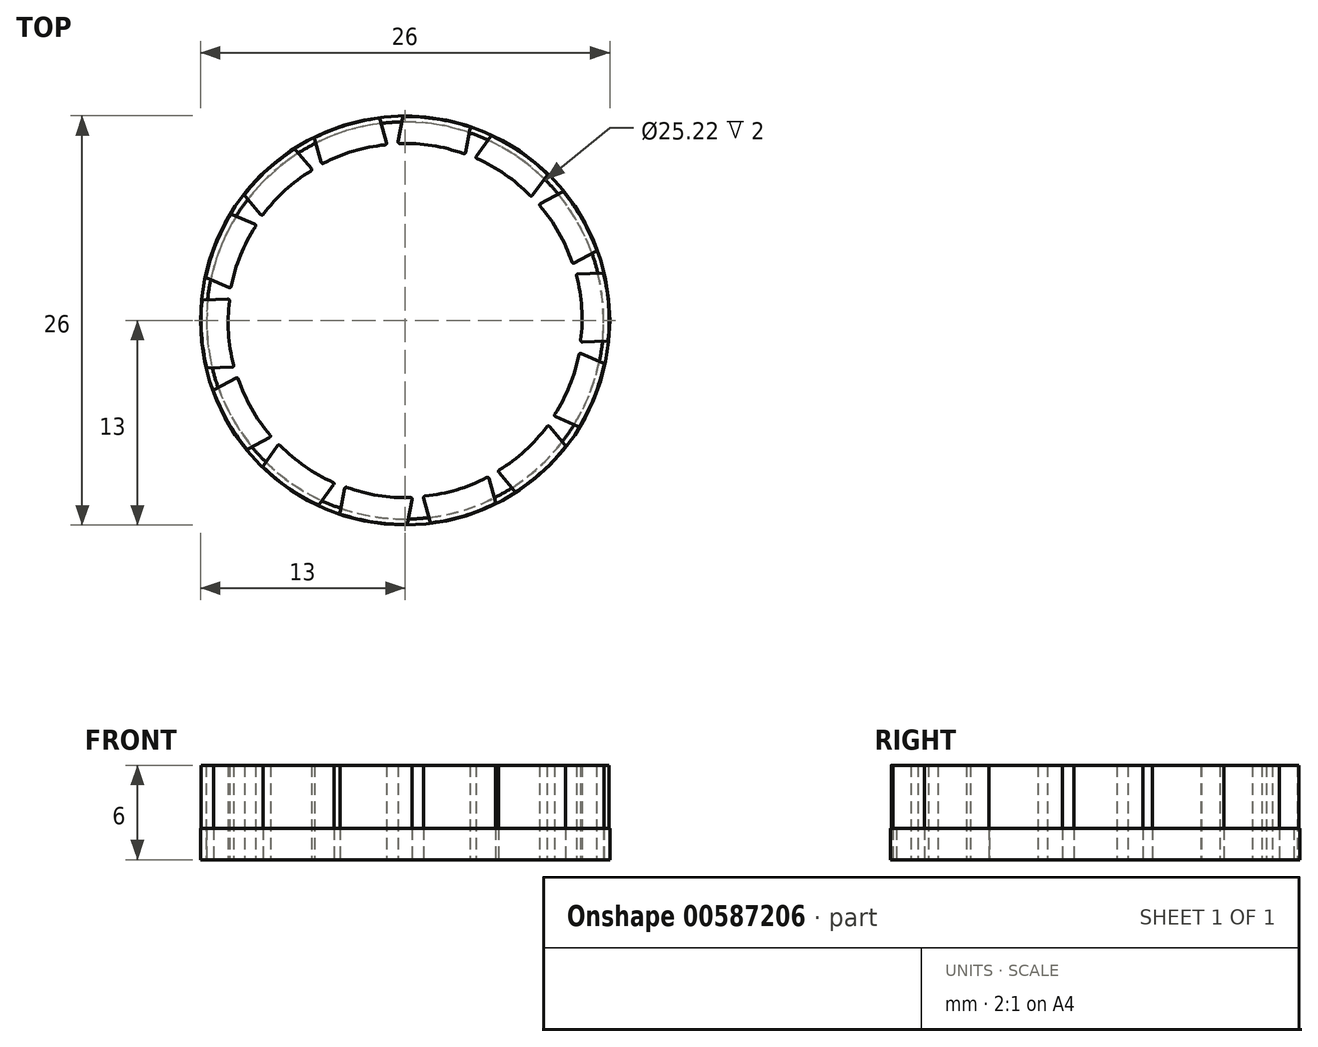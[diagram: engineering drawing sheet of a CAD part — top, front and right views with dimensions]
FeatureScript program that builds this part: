
annotation { "Feature Type Name" : "Feature", "Feature Type Description" : "" }
export const myFeature = defineFeature(function(context is Context, id is Id, definition is map)
    precondition{}
    {
        {
            var Q0;
            Q0=qCreatedBy(makeId("Top.planeOp"),FACE);
            var sketch = newSketch(context, id + "F0", { "sketchPlane" : qUnion([Q0])});
            skCircle(sketch, "E0", {"center": v(0, 0) * mm, "radius": 13.95 * mm});
            skCircle(sketch, "E1", {"center": v(0, 0) * mm, "radius": 4 * mm});
            skCircle(sketch, "E2", {"center": v(0, 0) * mm, "radius": 5.54 * mm, "construction": true});
            skArc(sketch, "E3", {"start": v(2.58, -4.9) * mm, "mid": v(0.81, -4.3) * mm, "end": v(-0.62, -5.5) * mm});
            skCircle(sketch, "E4", {"center": v(0, 0) * mm, "radius": 11.06 * mm, "construction": true});
            skCircle(sketch, "E5", {"center": v(0, 0) * mm, "radius": 13 * mm});
            skCircle(sketch, "E6", {"center": v(0, 0) * mm, "radius": 10.1 * mm, "construction": true});
            skLineSegment(sketch, "E7", {"start": v(2.58, -4.9) * mm, "end": v(4.91, -8.83) * mm});
            skLineSegment(sketch, "E8", {"start": v(0, 0) * mm, "end": v(1.16, -6.17) * mm});
            skLineSegment(sketch, "E9.MirrorCS", {"start": v(-0.62, -5.5) * mm, "end": v(-1.36, -10) * mm});
            skArc(sketch, "E10", {"start": v(-1.36, -10) * mm, "mid": v(-1.24, -10.63) * mm, "end": v(-0.75, -11.04) * mm});
            skArc(sketch, "E11.MirrorCS", {"start": v(4.91, -8.83) * mm, "mid": v(5.03, -9.45) * mm, "end": v(4.72, -10) * mm});
            skArc(sketch, "E12", {"start": v(-0.75, -11.04) * mm, "mid": v(2.05, -10.86) * mm, "end": v(4.72, -10) * mm});
            skLineSegment(sketch, "E13.1.0", {"start": v(3.46, -4.33) * mm, "end": v(6.12, -8.04) * mm});
            skArc(sketch, "E13.1.1", {"start": v(5.3, -1.64) * mm, "mid": v(3.62, -2.47) * mm, "end": v(3.46, -4.33) * mm});
            skLineSegment(sketch, "E13.1.2", {"start": v(5.3, -1.64) * mm, "end": v(9.71, -2.77) * mm});
            skArc(sketch, "E13.1.3", {"start": v(9.71, -2.77) * mm, "mid": v(10.24, -3.13) * mm, "end": v(10.4, -3.74) * mm});
            skArc(sketch, "E13.1.4", {"start": v(7.27, -8.33) * mm, "mid": v(9.13, -6.23) * mm, "end": v(10.4, -3.74) * mm});
            skArc(sketch, "E13.1.5", {"start": v(6.12, -8.04) * mm, "mid": v(6.64, -8.4) * mm, "end": v(7.27, -8.33) * mm});
            skLineSegment(sketch, "E13.2.0", {"start": v(5.5, -0.62) * mm, "end": v(10, -1.36) * mm});
            skArc(sketch, "E13.2.1", {"start": v(4.9, 2.58) * mm, "mid": v(4.3, 0.81) * mm, "end": v(5.5, -0.62) * mm});
            skLineSegment(sketch, "E13.2.2", {"start": v(4.9, 2.58) * mm, "end": v(8.83, 4.91) * mm});
            skArc(sketch, "E13.2.3", {"start": v(8.83, 4.91) * mm, "mid": v(9.45, 5.03) * mm, "end": v(10, 4.72) * mm});
            skArc(sketch, "E13.2.4", {"start": v(11.04, -0.75) * mm, "mid": v(10.86, 2.05) * mm, "end": v(10, 4.72) * mm});
            skArc(sketch, "E13.2.5", {"start": v(10, -1.36) * mm, "mid": v(10.63, -1.24) * mm, "end": v(11.04, -0.75) * mm});
            skLineSegment(sketch, "E13.3.0", {"start": v(4.33, 3.46) * mm, "end": v(8.04, 6.12) * mm});
            skArc(sketch, "E13.3.1", {"start": v(1.64, 5.3) * mm, "mid": v(2.47, 3.62) * mm, "end": v(4.33, 3.46) * mm});
            skLineSegment(sketch, "E13.3.2", {"start": v(1.64, 5.3) * mm, "end": v(2.77, 9.71) * mm});
            skArc(sketch, "E13.3.3", {"start": v(2.77, 9.71) * mm, "mid": v(3.13, 10.24) * mm, "end": v(3.74, 10.4) * mm});
            skArc(sketch, "E13.3.4", {"start": v(8.33, 7.27) * mm, "mid": v(6.23, 9.13) * mm, "end": v(3.74, 10.4) * mm});
            skArc(sketch, "E13.3.5", {"start": v(8.04, 6.12) * mm, "mid": v(8.4, 6.64) * mm, "end": v(8.33, 7.27) * mm});
            skLineSegment(sketch, "E13.4.0", {"start": v(0.62, 5.5) * mm, "end": v(1.36, 10) * mm});
            skArc(sketch, "E13.4.1", {"start": v(-2.58, 4.9) * mm, "mid": v(-0.81, 4.3) * mm, "end": v(0.62, 5.5) * mm});
            skLineSegment(sketch, "E13.4.2", {"start": v(-2.58, 4.9) * mm, "end": v(-4.91, 8.83) * mm});
            skArc(sketch, "E13.4.3", {"start": v(-4.91, 8.83) * mm, "mid": v(-5.03, 9.45) * mm, "end": v(-4.72, 10) * mm});
            skArc(sketch, "E13.4.4", {"start": v(0.75, 11.04) * mm, "mid": v(-2.05, 10.86) * mm, "end": v(-4.72, 10) * mm});
            skArc(sketch, "E13.4.5", {"start": v(1.36, 10) * mm, "mid": v(1.24, 10.63) * mm, "end": v(0.75, 11.04) * mm});
            skLineSegment(sketch, "E13.5.0", {"start": v(-3.46, 4.33) * mm, "end": v(-6.12, 8.04) * mm});
            skArc(sketch, "E13.5.1", {"start": v(-5.3, 1.64) * mm, "mid": v(-3.62, 2.47) * mm, "end": v(-3.46, 4.33) * mm});
            skLineSegment(sketch, "E13.5.2", {"start": v(-5.3, 1.64) * mm, "end": v(-9.71, 2.77) * mm});
            skArc(sketch, "E13.5.3", {"start": v(-9.71, 2.77) * mm, "mid": v(-10.24, 3.13) * mm, "end": v(-10.4, 3.74) * mm});
            skArc(sketch, "E13.5.4", {"start": v(-7.27, 8.33) * mm, "mid": v(-9.13, 6.23) * mm, "end": v(-10.4, 3.74) * mm});
            skArc(sketch, "E13.5.5", {"start": v(-6.12, 8.04) * mm, "mid": v(-6.64, 8.4) * mm, "end": v(-7.27, 8.33) * mm});
            skLineSegment(sketch, "E13.6.0", {"start": v(-5.5, 0.62) * mm, "end": v(-10, 1.36) * mm});
            skArc(sketch, "E13.6.1", {"start": v(-4.9, -2.58) * mm, "mid": v(-4.3, -0.81) * mm, "end": v(-5.5, 0.62) * mm});
            skLineSegment(sketch, "E13.6.2", {"start": v(-4.9, -2.58) * mm, "end": v(-8.83, -4.91) * mm});
            skArc(sketch, "E13.6.3", {"start": v(-8.83, -4.91) * mm, "mid": v(-9.45, -5.03) * mm, "end": v(-10, -4.72) * mm});
            skArc(sketch, "E13.6.4", {"start": v(-11.04, 0.75) * mm, "mid": v(-10.86, -2.05) * mm, "end": v(-10, -4.72) * mm});
            skArc(sketch, "E13.6.5", {"start": v(-10, 1.36) * mm, "mid": v(-10.63, 1.24) * mm, "end": v(-11.04, 0.75) * mm});
            skLineSegment(sketch, "E13.7.0", {"start": v(-4.33, -3.46) * mm, "end": v(-8.04, -6.12) * mm});
            skArc(sketch, "E13.7.1", {"start": v(-1.64, -5.3) * mm, "mid": v(-2.47, -3.62) * mm, "end": v(-4.33, -3.46) * mm});
            skLineSegment(sketch, "E13.7.2", {"start": v(-1.64, -5.3) * mm, "end": v(-2.77, -9.71) * mm});
            skArc(sketch, "E13.7.3", {"start": v(-2.77, -9.71) * mm, "mid": v(-3.13, -10.24) * mm, "end": v(-3.74, -10.4) * mm});
            skArc(sketch, "E13.7.4", {"start": v(-8.33, -7.27) * mm, "mid": v(-6.23, -9.13) * mm, "end": v(-3.74, -10.4) * mm});
            skArc(sketch, "E13.7.5", {"start": v(-8.04, -6.12) * mm, "mid": v(-8.4, -6.64) * mm, "end": v(-8.33, -7.27) * mm});
            skCircle(sketch, "E14", {"center": v(0, 0) * mm, "radius": 12.61 * mm});
            skSolve(sketch);
        }
        {
            var Q0;
            Q0=makeQuery(id+"F0.imprint","IMPRINT",FACE,{"disambiguationData":[TD([[makeQuery(id+"F0.imprint","IMPRINT",EDGE,{"derivedFrom":sQuery(id+"F0.wireOp",EDGE,"E0")}),1.0]])]});
            var sketch = newSketch(context, id + "F1", { "sketchPlane" : qUnion([Q0])});
            skArc(sketch, "E15", {"start": v(1.7, -12.85) * mm, "mid": v(3.74, -12.4) * mm, "end": v(5.68, -11.64) * mm});
            skArc(sketch, "E16", {"start": v(1.26, -11.15) * mm, "mid": v(3.28, -10.76) * mm, "end": v(5.2, -9.98) * mm});
            skLineSegment(sketch, "E17", {"start": v(1.17, -11.28) * mm, "end": v(1.58, -12.77) * mm});
            skLineSegment(sketch, "E18", {"start": v(5.33, -10.05) * mm, "end": v(5.73, -11.52) * mm});
            skPoint(sketch, "E19.visualSharp", {"position": v(1.14, -11.16) * mm});
            skArc(sketch, "E19.filletArc", {"start": v(1.26, -11.15) * mm, "mid": v(1.19, -11.2) * mm, "end": v(1.17, -11.28) * mm});
            skPoint(sketch, "E20.visualSharp", {"position": v(5.3, -9.93) * mm});
            skArc(sketch, "E20.filletArc", {"start": v(5.33, -10.05) * mm, "mid": v(5.28, -9.98) * mm, "end": v(5.2, -9.98) * mm});
            skPoint(sketch, "E21.visualSharp", {"position": v(5.76, -11.6) * mm});
            skArc(sketch, "E21.filletArc", {"start": v(5.68, -11.64) * mm, "mid": v(5.73, -11.6) * mm, "end": v(5.73, -11.52) * mm});
            skPoint(sketch, "E22.visualSharp", {"position": v(1.6, -12.86) * mm});
            skArc(sketch, "E22.filletArc", {"start": v(1.58, -12.77) * mm, "mid": v(1.62, -12.83) * mm, "end": v(1.7, -12.85) * mm});
            skLineSegment(sketch, "E23", {"start": v(3.28, -10.76) * mm, "end": v(3.74, -12.4) * mm, "construction": true});
            skLineSegment(sketch, "E24.1.0", {"start": v(7.62, -8.27) * mm, "end": v(8.75, -9.56) * mm, "construction": true});
            skPoint(sketch, "E24.1.1", {"position": v(7.02, -10.89) * mm});
            skArc(sketch, "E24.1.2", {"start": v(7.1, -10.84) * mm, "mid": v(8.75, -9.56) * mm, "end": v(10.17, -8.02) * mm});
            skPoint(sketch, "E24.1.3", {"position": v(10.22, -7.96) * mm});
            skLineSegment(sketch, "E24.1.4", {"start": v(9.16, -6.74) * mm, "end": v(10.17, -7.9) * mm});
            skLineSegment(sketch, "E24.1.5", {"start": v(5.95, -9.65) * mm, "end": v(6.97, -10.82) * mm});
            skArc(sketch, "E24.1.6", {"start": v(5.98, -9.5) * mm, "mid": v(7.62, -8.27) * mm, "end": v(9, -6.74) * mm});
            skPoint(sketch, "E24.1.7", {"position": v(9.08, -6.64) * mm});
            skPoint(sketch, "E24.1.8", {"position": v(5.87, -9.56) * mm});
            skArc(sketch, "E24.1.9", {"start": v(10.17, -8.02) * mm, "mid": v(10.2, -7.96) * mm, "end": v(10.17, -7.9) * mm});
            skArc(sketch, "E24.1.10", {"start": v(5.98, -9.5) * mm, "mid": v(5.93, -9.57) * mm, "end": v(5.95, -9.65) * mm});
            skArc(sketch, "E24.1.11", {"start": v(6.97, -10.82) * mm, "mid": v(7.03, -10.86) * mm, "end": v(7.1, -10.84) * mm});
            skArc(sketch, "E24.1.12", {"start": v(9.16, -6.74) * mm, "mid": v(9.08, -6.7) * mm, "end": v(9, -6.74) * mm});
            skArc(sketch, "E24.1.13", {"start": v(9.16, -6.74) * mm, "mid": v(9.08, -6.7) * mm, "end": v(9, -6.74) * mm});
            skLineSegment(sketch, "E24.2.0", {"start": v(10.46, -4.14) * mm, "end": v(12.03, -4.81) * mm, "construction": true});
            skPoint(sketch, "E24.2.1", {"position": v(11.05, -6.76) * mm});
            skArc(sketch, "E24.2.2", {"start": v(11.1, -6.69) * mm, "mid": v(12.03, -4.81) * mm, "end": v(12.64, -2.81) * mm});
            skPoint(sketch, "E24.2.3", {"position": v(12.66, -2.73) * mm});
            skLineSegment(sketch, "E24.2.4", {"start": v(11.18, -2.1) * mm, "end": v(12.58, -2.7) * mm});
            skLineSegment(sketch, "E24.2.5", {"start": v(9.55, -6.11) * mm, "end": v(10.97, -6.73) * mm});
            skArc(sketch, "E24.2.6", {"start": v(9.5, -5.97) * mm, "mid": v(10.46, -4.14) * mm, "end": v(11.04, -2.17) * mm});
            skPoint(sketch, "E24.2.7", {"position": v(11.06, -2.04) * mm});
            skPoint(sketch, "E24.2.8", {"position": v(9.44, -6.07) * mm});
            skArc(sketch, "E24.2.9", {"start": v(12.64, -2.81) * mm, "mid": v(12.63, -2.75) * mm, "end": v(12.58, -2.7) * mm});
            skArc(sketch, "E24.2.10", {"start": v(9.5, -5.97) * mm, "mid": v(9.5, -6.05) * mm, "end": v(9.55, -6.11) * mm});
            skArc(sketch, "E24.2.11", {"start": v(10.97, -6.73) * mm, "mid": v(11.04, -6.73) * mm, "end": v(11.1, -6.69) * mm});
            skArc(sketch, "E24.2.12", {"start": v(11.18, -2.1) * mm, "mid": v(11.1, -2.1) * mm, "end": v(11.04, -2.17) * mm});
            skArc(sketch, "E24.2.13", {"start": v(11.18, -2.1) * mm, "mid": v(11.1, -2.1) * mm, "end": v(11.04, -2.17) * mm});
            skLineSegment(sketch, "E24.3.0", {"start": v(11.22, 0.8) * mm, "end": v(12.93, 0.88) * mm, "construction": true});
            skPoint(sketch, "E24.3.1", {"position": v(12.9, -1.3) * mm});
            skArc(sketch, "E24.3.2", {"start": v(12.9, -1.21) * mm, "mid": v(12.93, 0.88) * mm, "end": v(12.61, 2.95) * mm});
            skPoint(sketch, "E24.3.3", {"position": v(12.6, 3.03) * mm});
            skLineSegment(sketch, "E24.3.4", {"start": v(10.98, 2.96) * mm, "end": v(12.51, 3.03) * mm});
            skLineSegment(sketch, "E24.3.5", {"start": v(11.26, -1.36) * mm, "end": v(12.8, -1.3) * mm});
            skArc(sketch, "E24.3.6", {"start": v(11.15, -1.25) * mm, "mid": v(11.22, 0.8) * mm, "end": v(10.89, 2.84) * mm});
            skPoint(sketch, "E24.3.7", {"position": v(10.86, 2.96) * mm});
            skPoint(sketch, "E24.3.8", {"position": v(11.14, -1.37) * mm});
            skArc(sketch, "E24.3.9", {"start": v(12.61, 2.95) * mm, "mid": v(12.57, 3) * mm, "end": v(12.51, 3.03) * mm});
            skArc(sketch, "E24.3.10", {"start": v(11.15, -1.25) * mm, "mid": v(11.18, -1.33) * mm, "end": v(11.26, -1.36) * mm});
            skArc(sketch, "E24.3.11", {"start": v(12.8, -1.3) * mm, "mid": v(12.87, -1.27) * mm, "end": v(12.9, -1.21) * mm});
            skArc(sketch, "E24.3.12", {"start": v(10.98, 2.96) * mm, "mid": v(10.9, 2.92) * mm, "end": v(10.89, 2.84) * mm});
            skArc(sketch, "E24.3.13", {"start": v(10.98, 2.96) * mm, "mid": v(10.9, 2.92) * mm, "end": v(10.89, 2.84) * mm});
            skLineSegment(sketch, "E24.4.0", {"start": v(9.76, 5.6) * mm, "end": v(11.27, 6.4) * mm, "construction": true});
            skPoint(sketch, "E24.4.1", {"position": v(12.18, 4.42) * mm});
            skArc(sketch, "E24.4.2", {"start": v(12.15, 4.5) * mm, "mid": v(11.27, 6.4) * mm, "end": v(10.08, 8.13) * mm});
            skPoint(sketch, "E24.4.3", {"position": v(10.03, 8.2) * mm});
            skLineSegment(sketch, "E24.4.4", {"start": v(8.6, 7.43) * mm, "end": v(9.96, 8.16) * mm});
            skLineSegment(sketch, "E24.4.5", {"start": v(10.74, 3.66) * mm, "end": v(12.1, 4.38) * mm});
            skArc(sketch, "E24.4.6", {"start": v(10.6, 3.71) * mm, "mid": v(9.76, 5.6) * mm, "end": v(8.58, 7.28) * mm});
            skPoint(sketch, "E24.4.7", {"position": v(8.5, 7.38) * mm});
            skPoint(sketch, "E24.4.8", {"position": v(10.63, 3.6) * mm});
            skArc(sketch, "E24.4.9", {"start": v(10.08, 8.13) * mm, "mid": v(10.02, 8.17) * mm, "end": v(9.96, 8.16) * mm});
            skArc(sketch, "E24.4.10", {"start": v(10.6, 3.71) * mm, "mid": v(10.65, 3.65) * mm, "end": v(10.74, 3.66) * mm});
            skArc(sketch, "E24.4.11", {"start": v(12.1, 4.38) * mm, "mid": v(12.15, 4.44) * mm, "end": v(12.15, 4.5) * mm});
            skArc(sketch, "E24.4.12", {"start": v(8.6, 7.43) * mm, "mid": v(8.56, 7.37) * mm, "end": v(8.58, 7.28) * mm});
            skArc(sketch, "E24.4.13", {"start": v(8.6, 7.43) * mm, "mid": v(8.56, 7.37) * mm, "end": v(8.58, 7.28) * mm});
            skLineSegment(sketch, "E24.5.0", {"start": v(6.36, 9.27) * mm, "end": v(7.37, 10.66) * mm, "construction": true});
            skPoint(sketch, "E24.5.1", {"position": v(9.05, 9.27) * mm});
            skArc(sketch, "E24.5.2", {"start": v(9, 9.33) * mm, "mid": v(7.37, 10.66) * mm, "end": v(5.56, 11.7) * mm});
            skPoint(sketch, "E24.5.3", {"position": v(5.48, 11.73) * mm});
            skLineSegment(sketch, "E24.5.4", {"start": v(4.53, 10.43) * mm, "end": v(5.43, 11.67) * mm});
            skLineSegment(sketch, "E24.5.5", {"start": v(8.09, 7.95) * mm, "end": v(9, 9.2) * mm});
            skArc(sketch, "E24.5.6", {"start": v(7.93, 7.94) * mm, "mid": v(6.36, 9.27) * mm, "end": v(4.57, 10.28) * mm});
            skPoint(sketch, "E24.5.7", {"position": v(4.45, 10.33) * mm});
            skPoint(sketch, "E24.5.8", {"position": v(8.02, 7.86) * mm});
            skArc(sketch, "E24.5.9", {"start": v(5.56, 11.7) * mm, "mid": v(5.49, 11.7) * mm, "end": v(5.43, 11.67) * mm});
            skArc(sketch, "E24.5.10", {"start": v(7.93, 7.94) * mm, "mid": v(8.01, 7.91) * mm, "end": v(8.09, 7.95) * mm});
            skArc(sketch, "E24.5.11", {"start": v(9, 9.2) * mm, "mid": v(9.02, 9.27) * mm, "end": v(9, 9.33) * mm});
            skArc(sketch, "E24.5.12", {"start": v(4.53, 10.43) * mm, "mid": v(4.51, 10.35) * mm, "end": v(4.57, 10.28) * mm});
            skArc(sketch, "E24.5.13", {"start": v(4.53, 10.43) * mm, "mid": v(4.51, 10.35) * mm, "end": v(4.57, 10.28) * mm});
            skLineSegment(sketch, "E24.6.0", {"start": v(1.71, 11.12) * mm, "end": v(2.02, 12.8) * mm, "construction": true});
            skPoint(sketch, "E24.6.1", {"position": v(4.13, 12.28) * mm});
            skArc(sketch, "E24.6.2", {"start": v(4.05, 12.3) * mm, "mid": v(2.02, 12.8) * mm, "end": v(-0.07, 12.95) * mm});
            skPoint(sketch, "E24.6.3", {"position": v(-0.15, 12.95) * mm});
            skLineSegment(sketch, "E24.6.4", {"start": v(-0.45, 11.36) * mm, "end": v(-0.17, 12.87) * mm});
            skLineSegment(sketch, "E24.6.5", {"start": v(3.84, 10.67) * mm, "end": v(4.12, 12.2) * mm});
            skArc(sketch, "E24.6.6", {"start": v(3.7, 10.6) * mm, "mid": v(1.71, 11.12) * mm, "end": v(-0.35, 11.25) * mm});
            skPoint(sketch, "E24.6.7", {"position": v(-0.47, 11.24) * mm});
            skPoint(sketch, "E24.6.8", {"position": v(3.81, 10.56) * mm});
            skArc(sketch, "E24.6.9", {"start": v(-0.07, 12.95) * mm, "mid": v(-0.13, 12.93) * mm, "end": v(-0.17, 12.87) * mm});
            skArc(sketch, "E24.6.10", {"start": v(3.7, 10.6) * mm, "mid": v(3.79, 10.6) * mm, "end": v(3.84, 10.67) * mm});
            skArc(sketch, "E24.6.11", {"start": v(4.12, 12.2) * mm, "mid": v(4.1, 12.26) * mm, "end": v(4.05, 12.3) * mm});
            skArc(sketch, "E24.6.12", {"start": v(-0.45, 11.36) * mm, "mid": v(-0.42, 11.28) * mm, "end": v(-0.35, 11.25) * mm});
            skArc(sketch, "E24.6.13", {"start": v(-0.45, 11.36) * mm, "mid": v(-0.42, 11.28) * mm, "end": v(-0.35, 11.25) * mm});
            skLineSegment(sketch, "E24.7.0", {"start": v(-3.28, 10.76) * mm, "end": v(-3.74, 12.4) * mm, "construction": true});
            skPoint(sketch, "E24.7.1", {"position": v(-1.6, 12.86) * mm});
            skArc(sketch, "E24.7.2", {"start": v(-1.7, 12.85) * mm, "mid": v(-3.74, 12.4) * mm, "end": v(-5.68, 11.64) * mm});
            skPoint(sketch, "E24.7.3", {"position": v(-5.76, 11.6) * mm});
            skLineSegment(sketch, "E24.7.4", {"start": v(-5.33, 10.05) * mm, "end": v(-5.73, 11.52) * mm});
            skLineSegment(sketch, "E24.7.5", {"start": v(-1.17, 11.28) * mm, "end": v(-1.58, 12.77) * mm});
            skArc(sketch, "E24.7.6", {"start": v(-1.26, 11.15) * mm, "mid": v(-3.28, 10.76) * mm, "end": v(-5.2, 9.98) * mm});
            skPoint(sketch, "E24.7.7", {"position": v(-5.3, 9.93) * mm});
            skPoint(sketch, "E24.7.8", {"position": v(-1.14, 11.16) * mm});
            skArc(sketch, "E24.7.9", {"start": v(-5.68, 11.64) * mm, "mid": v(-5.73, 11.6) * mm, "end": v(-5.73, 11.52) * mm});
            skArc(sketch, "E24.7.10", {"start": v(-1.26, 11.15) * mm, "mid": v(-1.19, 11.2) * mm, "end": v(-1.17, 11.28) * mm});
            skArc(sketch, "E24.7.11", {"start": v(-1.58, 12.77) * mm, "mid": v(-1.62, 12.83) * mm, "end": v(-1.7, 12.85) * mm});
            skArc(sketch, "E24.7.12", {"start": v(-5.33, 10.05) * mm, "mid": v(-5.28, 9.98) * mm, "end": v(-5.2, 9.98) * mm});
            skArc(sketch, "E24.7.13", {"start": v(-5.33, 10.05) * mm, "mid": v(-5.28, 9.98) * mm, "end": v(-5.2, 9.98) * mm});
            skLineSegment(sketch, "E24.8.0", {"start": v(-7.62, 8.27) * mm, "end": v(-8.75, 9.56) * mm, "construction": true});
            skPoint(sketch, "E24.8.1", {"position": v(-7.02, 10.89) * mm});
            skArc(sketch, "E24.8.2", {"start": v(-7.1, 10.84) * mm, "mid": v(-8.75, 9.56) * mm, "end": v(-10.17, 8.02) * mm});
            skPoint(sketch, "E24.8.3", {"position": v(-10.22, 7.96) * mm});
            skLineSegment(sketch, "E24.8.4", {"start": v(-9.16, 6.74) * mm, "end": v(-10.17, 7.9) * mm});
            skLineSegment(sketch, "E24.8.5", {"start": v(-5.95, 9.65) * mm, "end": v(-6.97, 10.82) * mm});
            skArc(sketch, "E24.8.6", {"start": v(-5.98, 9.5) * mm, "mid": v(-7.62, 8.27) * mm, "end": v(-9, 6.74) * mm});
            skPoint(sketch, "E24.8.7", {"position": v(-9.08, 6.64) * mm});
            skPoint(sketch, "E24.8.8", {"position": v(-5.87, 9.56) * mm});
            skArc(sketch, "E24.8.9", {"start": v(-10.17, 8.02) * mm, "mid": v(-10.2, 7.96) * mm, "end": v(-10.17, 7.9) * mm});
            skArc(sketch, "E24.8.10", {"start": v(-5.98, 9.5) * mm, "mid": v(-5.93, 9.57) * mm, "end": v(-5.95, 9.65) * mm});
            skArc(sketch, "E24.8.11", {"start": v(-6.97, 10.82) * mm, "mid": v(-7.03, 10.86) * mm, "end": v(-7.1, 10.84) * mm});
            skArc(sketch, "E24.8.12", {"start": v(-9.16, 6.74) * mm, "mid": v(-9.08, 6.7) * mm, "end": v(-9, 6.74) * mm});
            skArc(sketch, "E24.8.13", {"start": v(-9.16, 6.74) * mm, "mid": v(-9.08, 6.7) * mm, "end": v(-9, 6.74) * mm});
            skLineSegment(sketch, "E24.9.0", {"start": v(-10.46, 4.14) * mm, "end": v(-12.03, 4.81) * mm, "construction": true});
            skPoint(sketch, "E24.9.1", {"position": v(-11.05, 6.76) * mm});
            skArc(sketch, "E24.9.2", {"start": v(-11.1, 6.69) * mm, "mid": v(-12.03, 4.81) * mm, "end": v(-12.64, 2.81) * mm});
            skPoint(sketch, "E24.9.3", {"position": v(-12.66, 2.73) * mm});
            skLineSegment(sketch, "E24.9.4", {"start": v(-11.18, 2.1) * mm, "end": v(-12.58, 2.7) * mm});
            skLineSegment(sketch, "E24.9.5", {"start": v(-9.55, 6.11) * mm, "end": v(-10.97, 6.73) * mm});
            skArc(sketch, "E24.9.6", {"start": v(-9.5, 5.97) * mm, "mid": v(-10.46, 4.14) * mm, "end": v(-11.04, 2.17) * mm});
            skPoint(sketch, "E24.9.7", {"position": v(-11.06, 2.04) * mm});
            skPoint(sketch, "E24.9.8", {"position": v(-9.44, 6.07) * mm});
            skArc(sketch, "E24.9.9", {"start": v(-12.64, 2.81) * mm, "mid": v(-12.63, 2.75) * mm, "end": v(-12.58, 2.7) * mm});
            skArc(sketch, "E24.9.10", {"start": v(-9.5, 5.97) * mm, "mid": v(-9.5, 6.05) * mm, "end": v(-9.55, 6.11) * mm});
            skArc(sketch, "E24.9.11", {"start": v(-10.97, 6.73) * mm, "mid": v(-11.04, 6.73) * mm, "end": v(-11.1, 6.69) * mm});
            skArc(sketch, "E24.9.12", {"start": v(-11.18, 2.1) * mm, "mid": v(-11.1, 2.1) * mm, "end": v(-11.04, 2.17) * mm});
            skArc(sketch, "E24.9.13", {"start": v(-11.18, 2.1) * mm, "mid": v(-11.1, 2.1) * mm, "end": v(-11.04, 2.17) * mm});
            skLineSegment(sketch, "E24.10.0", {"start": v(-11.22, -0.8) * mm, "end": v(-12.93, -0.88) * mm, "construction": true});
            skPoint(sketch, "E24.10.1", {"position": v(-12.9, 1.3) * mm});
            skArc(sketch, "E24.10.2", {"start": v(-12.9, 1.21) * mm, "mid": v(-12.93, -0.88) * mm, "end": v(-12.61, -2.95) * mm});
            skPoint(sketch, "E24.10.3", {"position": v(-12.6, -3.03) * mm});
            skLineSegment(sketch, "E24.10.4", {"start": v(-10.98, -2.96) * mm, "end": v(-12.51, -3.03) * mm});
            skLineSegment(sketch, "E24.10.5", {"start": v(-11.26, 1.36) * mm, "end": v(-12.8, 1.3) * mm});
            skArc(sketch, "E24.10.6", {"start": v(-11.15, 1.25) * mm, "mid": v(-11.22, -0.8) * mm, "end": v(-10.89, -2.84) * mm});
            skPoint(sketch, "E24.10.7", {"position": v(-10.86, -2.96) * mm});
            skPoint(sketch, "E24.10.8", {"position": v(-11.14, 1.37) * mm});
            skArc(sketch, "E24.10.9", {"start": v(-12.61, -2.95) * mm, "mid": v(-12.57, -3) * mm, "end": v(-12.51, -3.03) * mm});
            skArc(sketch, "E24.10.10", {"start": v(-11.15, 1.25) * mm, "mid": v(-11.18, 1.33) * mm, "end": v(-11.26, 1.36) * mm});
            skArc(sketch, "E24.10.11", {"start": v(-12.8, 1.3) * mm, "mid": v(-12.87, 1.27) * mm, "end": v(-12.9, 1.21) * mm});
            skArc(sketch, "E24.10.12", {"start": v(-10.98, -2.96) * mm, "mid": v(-10.9, -2.92) * mm, "end": v(-10.89, -2.84) * mm});
            skArc(sketch, "E24.10.13", {"start": v(-10.98, -2.96) * mm, "mid": v(-10.9, -2.92) * mm, "end": v(-10.89, -2.84) * mm});
            skLineSegment(sketch, "E24.11.0", {"start": v(-9.76, -5.6) * mm, "end": v(-11.27, -6.4) * mm, "construction": true});
            skPoint(sketch, "E24.11.1", {"position": v(-12.18, -4.42) * mm});
            skArc(sketch, "E24.11.2", {"start": v(-12.15, -4.5) * mm, "mid": v(-11.27, -6.4) * mm, "end": v(-10.08, -8.13) * mm});
            skPoint(sketch, "E24.11.3", {"position": v(-10.03, -8.2) * mm});
            skLineSegment(sketch, "E24.11.4", {"start": v(-8.6, -7.43) * mm, "end": v(-9.96, -8.16) * mm});
            skLineSegment(sketch, "E24.11.5", {"start": v(-10.74, -3.66) * mm, "end": v(-12.1, -4.38) * mm});
            skArc(sketch, "E24.11.6", {"start": v(-10.6, -3.71) * mm, "mid": v(-9.76, -5.6) * mm, "end": v(-8.58, -7.28) * mm});
            skPoint(sketch, "E24.11.7", {"position": v(-8.5, -7.38) * mm});
            skPoint(sketch, "E24.11.8", {"position": v(-10.63, -3.6) * mm});
            skArc(sketch, "E24.11.9", {"start": v(-10.08, -8.13) * mm, "mid": v(-10.02, -8.17) * mm, "end": v(-9.96, -8.16) * mm});
            skArc(sketch, "E24.11.10", {"start": v(-10.6, -3.71) * mm, "mid": v(-10.65, -3.65) * mm, "end": v(-10.74, -3.66) * mm});
            skArc(sketch, "E24.11.11", {"start": v(-12.1, -4.38) * mm, "mid": v(-12.15, -4.44) * mm, "end": v(-12.15, -4.5) * mm});
            skArc(sketch, "E24.11.12", {"start": v(-8.6, -7.43) * mm, "mid": v(-8.56, -7.37) * mm, "end": v(-8.58, -7.28) * mm});
            skArc(sketch, "E24.11.13", {"start": v(-8.6, -7.43) * mm, "mid": v(-8.56, -7.37) * mm, "end": v(-8.58, -7.28) * mm});
            skLineSegment(sketch, "E24.12.0", {"start": v(-6.36, -9.27) * mm, "end": v(-7.37, -10.66) * mm, "construction": true});
            skPoint(sketch, "E24.12.1", {"position": v(-9.05, -9.27) * mm});
            skArc(sketch, "E24.12.2", {"start": v(-9, -9.33) * mm, "mid": v(-7.37, -10.66) * mm, "end": v(-5.56, -11.7) * mm});
            skPoint(sketch, "E24.12.3", {"position": v(-5.48, -11.73) * mm});
            skLineSegment(sketch, "E24.12.4", {"start": v(-4.53, -10.43) * mm, "end": v(-5.43, -11.67) * mm});
            skLineSegment(sketch, "E24.12.5", {"start": v(-8.09, -7.95) * mm, "end": v(-9, -9.2) * mm});
            skArc(sketch, "E24.12.6", {"start": v(-7.93, -7.94) * mm, "mid": v(-6.36, -9.27) * mm, "end": v(-4.57, -10.28) * mm});
            skPoint(sketch, "E24.12.7", {"position": v(-4.45, -10.33) * mm});
            skPoint(sketch, "E24.12.8", {"position": v(-8.02, -7.86) * mm});
            skArc(sketch, "E24.12.9", {"start": v(-5.56, -11.7) * mm, "mid": v(-5.49, -11.7) * mm, "end": v(-5.43, -11.67) * mm});
            skArc(sketch, "E24.12.10", {"start": v(-7.93, -7.94) * mm, "mid": v(-8.01, -7.91) * mm, "end": v(-8.09, -7.95) * mm});
            skArc(sketch, "E24.12.11", {"start": v(-9, -9.2) * mm, "mid": v(-9.02, -9.27) * mm, "end": v(-9, -9.33) * mm});
            skArc(sketch, "E24.12.12", {"start": v(-4.53, -10.43) * mm, "mid": v(-4.51, -10.35) * mm, "end": v(-4.57, -10.28) * mm});
            skArc(sketch, "E24.12.13", {"start": v(-4.53, -10.43) * mm, "mid": v(-4.51, -10.35) * mm, "end": v(-4.57, -10.28) * mm});
            skLineSegment(sketch, "E24.13.0", {"start": v(-1.71, -11.12) * mm, "end": v(-2.02, -12.8) * mm, "construction": true});
            skPoint(sketch, "E24.13.1", {"position": v(-4.13, -12.28) * mm});
            skArc(sketch, "E24.13.2", {"start": v(-4.05, -12.3) * mm, "mid": v(-2.02, -12.8) * mm, "end": v(0.07, -12.95) * mm});
            skPoint(sketch, "E24.13.3", {"position": v(0.15, -12.95) * mm});
            skLineSegment(sketch, "E24.13.4", {"start": v(0.45, -11.36) * mm, "end": v(0.17, -12.87) * mm});
            skLineSegment(sketch, "E24.13.5", {"start": v(-3.84, -10.67) * mm, "end": v(-4.12, -12.2) * mm});
            skArc(sketch, "E24.13.6", {"start": v(-3.7, -10.6) * mm, "mid": v(-1.71, -11.12) * mm, "end": v(0.35, -11.25) * mm});
            skPoint(sketch, "E24.13.7", {"position": v(0.47, -11.24) * mm});
            skPoint(sketch, "E24.13.8", {"position": v(-3.81, -10.56) * mm});
            skArc(sketch, "E24.13.9", {"start": v(0.07, -12.95) * mm, "mid": v(0.13, -12.93) * mm, "end": v(0.17, -12.87) * mm});
            skArc(sketch, "E24.13.10", {"start": v(-3.7, -10.6) * mm, "mid": v(-3.79, -10.6) * mm, "end": v(-3.84, -10.67) * mm});
            skArc(sketch, "E24.13.11", {"start": v(-4.12, -12.2) * mm, "mid": v(-4.1, -12.26) * mm, "end": v(-4.05, -12.3) * mm});
            skArc(sketch, "E24.13.12", {"start": v(0.45, -11.36) * mm, "mid": v(0.42, -11.28) * mm, "end": v(0.35, -11.25) * mm});
            skArc(sketch, "E24.13.13", {"start": v(0.45, -11.36) * mm, "mid": v(0.42, -11.28) * mm, "end": v(0.35, -11.25) * mm});
            skPoint(sketch, "E24.center", {"position": v(0, 0) * mm});
            skSolve(sketch);
        }
        {
            var Q0;
            Q0=makeQuery(id+"F1.imprint","IMPRINT",FACE,{"disambiguationData":[TD([[makeQuery(id+"F1.imprint","IMPRINT",EDGE,{"derivedFrom":sQuery(id+"F1.wireOp",EDGE,"E15")}),1.0]])]});
            var Q1;
            Q1=makeQuery(id+"F1.imprint","IMPRINT",FACE,{"disambiguationData":[TD([[makeQuery(id+"F1.imprint","IMPRINT",EDGE,{"derivedFrom":sQuery(id+"F1.wireOp",EDGE,"E24.13.2")}),1.0]])]});
            var Q2;
            Q2=makeQuery(id+"F1.imprint","IMPRINT",FACE,{"disambiguationData":[TD([[makeQuery(id+"F1.imprint","IMPRINT",EDGE,{"derivedFrom":sQuery(id+"F1.wireOp",EDGE,"E24.12.2")}),1.0]])]});
            var Q3;
            Q3=makeQuery(id+"F1.imprint","IMPRINT",FACE,{"disambiguationData":[TD([[makeQuery(id+"F1.imprint","IMPRINT",EDGE,{"derivedFrom":sQuery(id+"F1.wireOp",EDGE,"E24.1.2")}),1.0]])]});
            var Q4;
            Q4=makeQuery(id+"F1.imprint","IMPRINT",FACE,{"disambiguationData":[TD([[makeQuery(id+"F1.imprint","IMPRINT",EDGE,{"derivedFrom":sQuery(id+"F1.wireOp",EDGE,"E24.2.2")}),1.0]])]});
            var Q5;
            Q5=makeQuery(id+"F1.imprint","IMPRINT",FACE,{"disambiguationData":[TD([[makeQuery(id+"F1.imprint","IMPRINT",EDGE,{"derivedFrom":sQuery(id+"F1.wireOp",EDGE,"E24.3.2")}),1.0]])]});
            var Q6;
            Q6=makeQuery(id+"F1.imprint","IMPRINT",FACE,{"disambiguationData":[TD([[makeQuery(id+"F1.imprint","IMPRINT",EDGE,{"derivedFrom":sQuery(id+"F1.wireOp",EDGE,"E24.4.2")}),1.0]])]});
            var Q7;
            Q7=makeQuery(id+"F1.imprint","IMPRINT",FACE,{"disambiguationData":[TD([[makeQuery(id+"F1.imprint","IMPRINT",EDGE,{"derivedFrom":sQuery(id+"F1.wireOp",EDGE,"E24.5.2")}),1.0]])]});
            var Q8;
            Q8=makeQuery(id+"F1.imprint","IMPRINT",FACE,{"disambiguationData":[TD([[makeQuery(id+"F1.imprint","IMPRINT",EDGE,{"derivedFrom":sQuery(id+"F1.wireOp",EDGE,"E24.6.2")}),1.0]])]});
            var Q9;
            Q9=makeQuery(id+"F1.imprint","IMPRINT",FACE,{"disambiguationData":[TD([[makeQuery(id+"F1.imprint","IMPRINT",EDGE,{"derivedFrom":sQuery(id+"F1.wireOp",EDGE,"E24.7.2")}),1.0]])]});
            var Q10;
            Q10=makeQuery(id+"F1.imprint","IMPRINT",FACE,{"disambiguationData":[TD([[makeQuery(id+"F1.imprint","IMPRINT",EDGE,{"derivedFrom":sQuery(id+"F1.wireOp",EDGE,"E24.8.2")}),1.0]])]});
            var Q11;
            Q11=makeQuery(id+"F1.imprint","IMPRINT",FACE,{"disambiguationData":[TD([[makeQuery(id+"F1.imprint","IMPRINT",EDGE,{"derivedFrom":sQuery(id+"F1.wireOp",EDGE,"E24.9.2")}),1.0]])]});
            var Q12;
            Q12=makeQuery(id+"F1.imprint","IMPRINT",FACE,{"disambiguationData":[TD([[makeQuery(id+"F1.imprint","IMPRINT",EDGE,{"derivedFrom":sQuery(id+"F1.wireOp",EDGE,"E24.10.2")}),1.0]])]});
            var Q13;
            Q13=makeQuery(id+"F1.imprint","IMPRINT",FACE,{"disambiguationData":[TD([[makeQuery(id+"F1.imprint","IMPRINT",EDGE,{"derivedFrom":sQuery(id+"F1.wireOp",EDGE,"E24.11.2")}),1.0]])]});
            extrude(context, id + "F2", {"entities" : qUnion([Q0, Q1, Q2, Q3, Q4, Q5, Q6, Q7, Q8, Q9, Q10, Q11, Q12, Q13]), "depth" : 6 * mm});
        }
        {
            var Q0;
            Q0=makeQuery(id+"F0.imprint","IMPRINT",FACE,{"disambiguationData":[TD([[makeQuery(id+"F0.imprint","IMPRINT",EDGE,{"derivedFrom":sQuery(id+"F0.wireOp",EDGE,"E5")}),1.0]])]});
            extrude(context, id + "F3", {"entities" : qUnion([Q0]), "depth" : 2 * mm});
        }
    });
